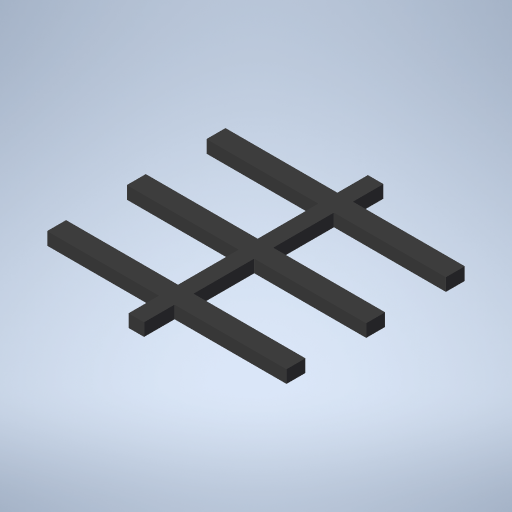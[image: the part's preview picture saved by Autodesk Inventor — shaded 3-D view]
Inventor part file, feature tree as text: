
AUTODESK INVENTOR PART (.ipt)
format: ipt  version: 2024.3 (Build 283343000, 343)  size: 282,624 bytes
history: native  units: mm
features: extrude x2, mirror x2, sketch x1
ambient origin geometry x8: Origin, YZ Plane, XZ Plane, XY Plane, X Axis, Y Axis, Z Axis, Center Point
bodies: Solid1 (feature_tree)
feature tree (5):
  sketch  "Sketch1"  dims[d0=94.0mm d1=94.0mm d2=12.0mm d3=24.0mm d4=7.333mm d5=5.0mm d6=0.0mm d7=5.0mm d8=0.0mm d9=3.0mm d10=0.0mm]
  extrude  "Extrusion1"  Depth=94.0mm
  extrude  "Extrusion2"  Depth=12.0mm
  mirror  "Mirror1"
  mirror  "Mirror2"
